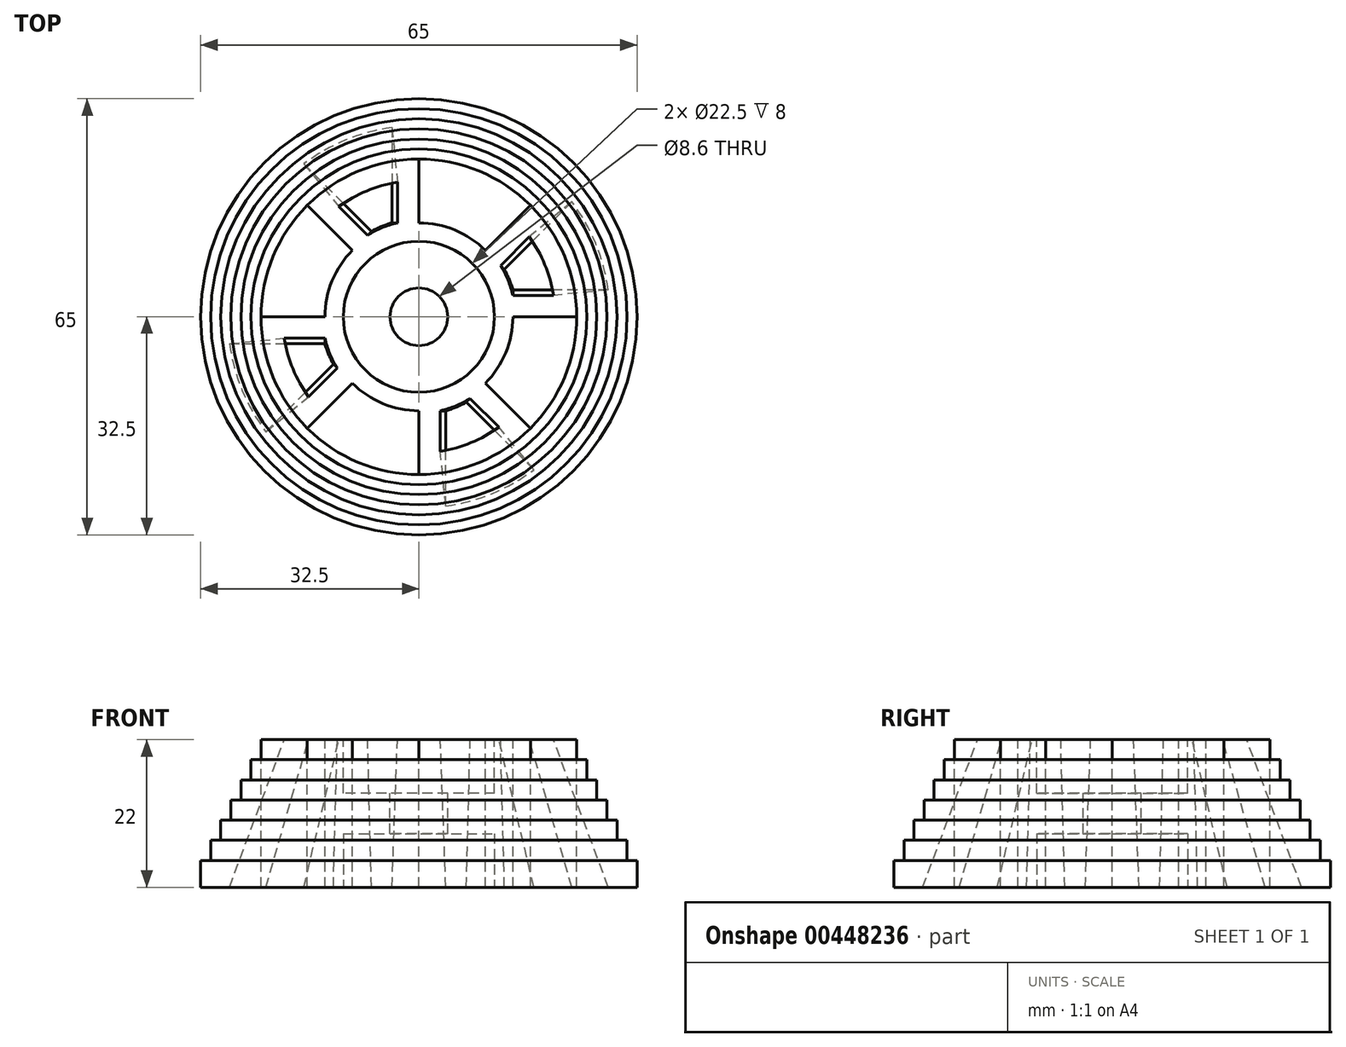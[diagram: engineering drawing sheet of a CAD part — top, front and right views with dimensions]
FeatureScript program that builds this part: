
annotation { "Feature Type Name" : "Feature", "Feature Type Description" : "" }
export const myFeature = defineFeature(function(context is Context, id is Id, definition is map)
    precondition{}
    {
        {
            var Q0;
            Q0=qCreatedBy(makeId("Top.planeOp"),FACE);
            var sketch = newSketch(context, id + "F0", { "sketchPlane" : qUnion([Q0])});
            skCircle(sketch, "E0", {"center": v(0, 0) * mm, "radius": 32.5 * mm});
            skCircle(sketch, "E1.0", {"center": v(0, 0) * mm, "radius": 31 * mm});
            skCircle(sketch, "E2.0", {"center": v(0, 0) * mm, "radius": 29.5 * mm});
            skCircle(sketch, "E3.0", {"center": v(0, 0) * mm, "radius": 28 * mm});
            skCircle(sketch, "E4.0", {"center": v(0, 0) * mm, "radius": 26.5 * mm});
            skCircle(sketch, "E5.0", {"center": v(0, 0) * mm, "radius": 25 * mm});
            skCircle(sketch, "E6.0", {"center": v(0, 0) * mm, "radius": 23.5 * mm});
            skSolve(sketch);
        }
        {
            var Q0;
            Q0 = qSketchRegion(id + "F0", true);
            extrude(context, id + "F1", {"entities" : qUnion([Q0]), "depth" : 4 * mm, "offsetDistance" : 25 * mm});
        }
        {
            var Q0;
            Q0=makeQuery(id+"F0.imprint","IMPRINT",FACE,{"disambiguationData":[TD([[makeQuery(id+"F0.imprint","IMPRINT",EDGE,{"derivedFrom":sQuery(id+"F0.wireOp",EDGE,"E1.0")}),1.0]])]});
            extrude(context, id + "F2", {"entities" : qUnion([Q0]), "operationType" : NewBodyOperationType.ADD, "depth" : 7 * mm, "offsetDistance" : 25 * mm});
        }
        {
            var Q0;
            Q0=makeQuery(id+"F0.imprint","IMPRINT",FACE,{"disambiguationData":[TD([[makeQuery(id+"F0.imprint","IMPRINT",EDGE,{"derivedFrom":sQuery(id+"F0.wireOp",EDGE,"E2.0")}),1.0]])]});
            extrude(context, id + "F3", {"entities" : qUnion([Q0]), "operationType" : NewBodyOperationType.ADD, "depth" : 10 * mm, "offsetDistance" : 25 * mm});
        }
        {
            var Q0;
            Q0=makeQuery(id+"F0.imprint","IMPRINT",FACE,{"disambiguationData":[TD([[makeQuery(id+"F0.imprint","IMPRINT",EDGE,{"derivedFrom":sQuery(id+"F0.wireOp",EDGE,"E3.0")}),1.0]])]});
            extrude(context, id + "F4", {"entities" : qUnion([Q0]), "operationType" : NewBodyOperationType.ADD, "depth" : 13 * mm, "offsetDistance" : 25 * mm});
        }
        {
            var Q0;
            Q0=makeQuery(id+"F0.imprint","IMPRINT",FACE,{"disambiguationData":[TD([[makeQuery(id+"F0.imprint","IMPRINT",EDGE,{"derivedFrom":sQuery(id+"F0.wireOp",EDGE,"E4.0")}),1.0]])]});
            extrude(context, id + "F5", {"entities" : qUnion([Q0]), "operationType" : NewBodyOperationType.ADD, "depth" : 16 * mm, "offsetDistance" : 25 * mm});
        }
        {
            var Q0;
            Q0=makeQuery(id+"F0.imprint","IMPRINT",FACE,{"disambiguationData":[TD([[makeQuery(id+"F0.imprint","IMPRINT",EDGE,{"derivedFrom":sQuery(id+"F0.wireOp",EDGE,"E5.0")}),1.0]])]});
            extrude(context, id + "F6", {"entities" : qUnion([Q0]), "operationType" : NewBodyOperationType.ADD, "depth" : 19 * mm, "offsetDistance" : 25 * mm});
        }
        {
            var Q0;
            Q0=makeQuery(id+"F0.imprint","IMPRINT",FACE,{"disambiguationData":[TD([[makeQuery(id+"F0.imprint","IMPRINT",EDGE,{"derivedFrom":sQuery(id+"F0.wireOp",EDGE,"E6.0")}),1.0]])]});
            extrude(context, id + "F7", {"entities" : qUnion([Q0]), "operationType" : NewBodyOperationType.ADD, "depth" : 22 * mm, "offsetDistance" : 25 * mm});
        }
        {
            var Q0;
            Q0=makeQuery(id+"F7.opExtrude","CAP_FACE",FACE,{"disambiguationData":[OSD([sQuery(id+"F0.wireOp",EDGE,"E6.0")])],"isStart":false});
            var sketch = newSketch(context, id + "F8", { "sketchPlane" : qUnion([Q0])});
            skCircle(sketch, "E7", {"center": v(0, 0) * mm, "radius": 14 * mm});
            skLineSegment(sketch, "E8", {"start": v(0, 0) * mm, "end": v(-25.46, 25.46) * mm, "construction": true});
            skLineSegment(sketch, "E9", {"start": v(-9.9, 9.9) * mm, "end": v(-25.46, 25.46) * mm});
            skLineSegment(sketch, "E10", {"start": v(-36, 0) * mm, "end": v(-14, 0) * mm});
            skArc(sketch, "E11", {"start": v(-36, 0) * mm, "mid": v(-33.26, 13.78) * mm, "end": v(-25.46, 25.46) * mm});
            skLineSegment(sketch, "E12.1.0", {"start": v(0, 0) * mm, "end": v(-25.46, -25.46) * mm, "construction": true});
            skLineSegment(sketch, "E12.2.0", {"start": v(0, 0) * mm, "end": v(25.46, -25.46) * mm, "construction": true});
            skLineSegment(sketch, "E13.1.0", {"start": v(0, -36) * mm, "end": v(0, -14) * mm});
            skLineSegment(sketch, "E13.2.0", {"start": v(36, 0) * mm, "end": v(14, 0) * mm});
            skLineSegment(sketch, "E14.2.3.0", {"start": v(0, 0) * mm, "end": v(25.46, 25.46) * mm, "construction": true});
            skLineSegment(sketch, "E15.1.3.0", {"start": v(0, 36) * mm, "end": v(0, 14) * mm});
            skArc(sketch, "E16", {"start": v(0, 36) * mm, "mid": v(13.78, 33.26) * mm, "end": v(25.46, 25.46) * mm});
            skArc(sketch, "E17", {"start": v(36, 0) * mm, "mid": v(33.26, -13.78) * mm, "end": v(25.46, -25.46) * mm});
            skArc(sketch, "E18", {"start": v(0, -36) * mm, "mid": v(-13.78, -33.26) * mm, "end": v(-25.46, -25.46) * mm});
            skLineSegment(sketch, "E19", {"start": v(9.9, 9.9) * mm, "end": v(25.46, 25.46) * mm});
            skLineSegment(sketch, "E20", {"start": v(9.9, -9.9) * mm, "end": v(25.46, -25.46) * mm});
            skLineSegment(sketch, "E21", {"start": v(-9.9, -9.9) * mm, "end": v(-25.46, -25.46) * mm});
            skSolve(sketch);
        }
        {
            var Q0;
            {var subQ0=sQuery(id+"F8.wireOp",EDGE,"E11");Q0=makeQuery(id+"F8.imprint","IMPRINT",FACE,{"disambiguationData":[TD([[makeQuery(id+"F8.imprint","IMPRINT",EDGE,{"derivedFrom":subQ0}),-1.0]])]});}
            var Q1;
            {var subQ0=sQuery(id+"F8.wireOp",EDGE,"E9");var subQ1=sQuery(id+"F8.wireOp",EDGE,"E7");var subQ2=makeQuery(id+"F8.imprint","INTERSECT",VERTEX,{"derivedFrom":[subQ1,subQ0]});Q1=makeQuery(id+"F8.imprint","IMPRINT",FACE,{"disambiguationData":[TD([[makeQuery(id+"F8.imprint","IMPRINT",EDGE,{"disambiguationData":[TD([[subQ2,-1.0]])],"derivedFrom":subQ1}),-1.0]])]});}
            var Q2;
            {var subQ0=sQuery(id+"F8.wireOp",EDGE,"E15.1.3.0");var subQ1=sQuery(id+"F8.wireOp",EDGE,"E7");var subQ2=makeQuery(id+"F8.imprint","INTERSECT",VERTEX,{"derivedFrom":[subQ1,subQ0]});Q2=makeQuery(id+"F8.imprint","IMPRINT",FACE,{"disambiguationData":[TD([[makeQuery(id+"F8.imprint","IMPRINT",EDGE,{"disambiguationData":[TD([[subQ2,1.0]])],"derivedFrom":subQ1}),-1.0]])]});}
            var Q3;
            {var subQ0=sQuery(id+"F8.wireOp",EDGE,"E16");Q3=makeQuery(id+"F8.imprint","IMPRINT",FACE,{"disambiguationData":[TD([[makeQuery(id+"F8.imprint","IMPRINT",EDGE,{"derivedFrom":subQ0}),-1.0]])]});}
            var Q4;
            {var subQ0=sQuery(id+"F8.wireOp",EDGE,"E13.2.0");var subQ1=sQuery(id+"F8.wireOp",EDGE,"E7");var subQ2=makeQuery(id+"F8.imprint","INTERSECT",VERTEX,{"derivedFrom":[subQ1,subQ0]});Q4=makeQuery(id+"F8.imprint","IMPRINT",FACE,{"disambiguationData":[TD([[makeQuery(id+"F8.imprint","IMPRINT",EDGE,{"disambiguationData":[TD([[subQ2,1.0]])],"derivedFrom":subQ1}),-1.0]])]});}
            var Q5;
            {var subQ0=sQuery(id+"F8.wireOp",EDGE,"E17");Q5=makeQuery(id+"F8.imprint","IMPRINT",FACE,{"disambiguationData":[TD([[makeQuery(id+"F8.imprint","IMPRINT",EDGE,{"derivedFrom":subQ0}),-1.0]])]});}
            var Q6;
            {var subQ0=sQuery(id+"F8.wireOp",EDGE,"E13.1.0");var subQ1=sQuery(id+"F8.wireOp",EDGE,"E7");var subQ2=makeQuery(id+"F8.imprint","INTERSECT",VERTEX,{"derivedFrom":[subQ1,subQ0]});Q6=makeQuery(id+"F8.imprint","IMPRINT",FACE,{"disambiguationData":[TD([[makeQuery(id+"F8.imprint","IMPRINT",EDGE,{"disambiguationData":[TD([[subQ2,1.0]])],"derivedFrom":subQ1}),-1.0]])]});}
            var Q7;
            {var subQ0=sQuery(id+"F8.wireOp",EDGE,"E18");Q7=makeQuery(id+"F8.imprint","IMPRINT",FACE,{"disambiguationData":[TD([[makeQuery(id+"F8.imprint","IMPRINT",EDGE,{"derivedFrom":subQ0}),-1.0]])]});}
            extrude(context, id + "F9", {"entities" : qUnion([Q0, Q1, Q2, Q3, Q4, Q5, Q6, Q7]), "operationType" : NewBodyOperationType.REMOVE, "oppositeDirection" : true, "depth" : 25 * mm, "offsetDistance" : 25 * mm});
        }
        {
            var Q0;
            Q0=makeQuery(id+"F7.opExtrude","CAP_FACE",FACE,{"disambiguationData":[OSD([sQuery(id+"F0.wireOp",EDGE,"E6.0")])],"isStart":false});
            var sketch = newSketch(context, id + "F10", { "sketchPlane" : qUnion([Q0])});
            skPoint(sketch, "E22", {"position": v(0, 0) * mm});
            skSolve(sketch);
        }
        {
            var Q0;
            Q0=sQuery(id+"F10.wireOp",VERTEX,"E22");
            var Q1;
            Q1=makeQuery(id+"F1.opExtrude","SWEPT_BODY",BODY,{"disambiguationData":[OSD([sQuery(id+"F0.wireOp",EDGE,"E0"),sQuery(id+"F0.wireOp",EDGE,"E1.0")])]});
            hole(context, id + "F11", {"style" : HoleStyle.C_BORE, "endStyle" : HoleEndStyle.THROUGH, "holeDiameter" : 8.6 * mm, "cBoreDiameter" : 22.5 * mm, "cBoreDepth" : 8 * mm, "isTappedThrough" : true, "tappedDepth" : 12 * mm, "tapClearance" : 3, "locations" : qUnion([Q0]), "scope" : qUnion([Q1])});
        }
        {
            var Q0;
            {var subQ0=sQuery(id+"F0.wireOp",EDGE,"E6.0");var subQ1=sQuery(id+"F0.wireOp",EDGE,"E5.0");var subQ2=sQuery(id+"F0.wireOp",EDGE,"E4.0");var subQ3=sQuery(id+"F0.wireOp",EDGE,"E3.0");var subQ4=sQuery(id+"F0.wireOp",EDGE,"E2.0");var subQ5=sQuery(id+"F0.wireOp",EDGE,"E1.0");Q0=makeQuery(id+"F7.boolean.opBoolean","MERGE",FACE,{"derivedFrom":[makeQuery(id+"F6.boolean.opBoolean","MERGE",FACE,{"derivedFrom":[makeQuery(id+"F5.boolean.opBoolean","MERGE",FACE,{"derivedFrom":[makeQuery(id+"F4.boolean.opBoolean","MERGE",FACE,{"derivedFrom":[makeQuery(id+"F3.boolean.opBoolean","MERGE",FACE,{"derivedFrom":[makeQuery(id+"F2.boolean.opBoolean","MERGE",FACE,{"derivedFrom":[makeQuery(id+"F1.opExtrude","CAP_FACE",FACE,{"disambiguationData":[OSD([sQuery(id+"F0.wireOp",EDGE,"E0"),subQ5])],"isStart":true}),makeQuery(id+"F2.opExtrude","CAP_FACE",FACE,{"disambiguationData":[OSD([subQ5,subQ4])],"isStart":true})]}),makeQuery(id+"F3.opExtrude","CAP_FACE",FACE,{"disambiguationData":[OSD([subQ4,subQ3])],"isStart":true})]}),makeQuery(id+"F4.opExtrude","CAP_FACE",FACE,{"disambiguationData":[OSD([subQ3,subQ2])],"isStart":true})]}),makeQuery(id+"F5.opExtrude","CAP_FACE",FACE,{"disambiguationData":[OSD([subQ2,subQ1])],"isStart":true})]}),makeQuery(id+"F6.opExtrude","CAP_FACE",FACE,{"disambiguationData":[OSD([subQ1,subQ0])],"isStart":true})]}),makeQuery(id+"F7.opExtrude","CAP_FACE",FACE,{"disambiguationData":[OSD([subQ0])],"isStart":true})]});}
            var sketch = newSketch(context, id + "F12", { "sketchPlane" : qUnion([Q0])});
            skPoint(sketch, "E23", {"position": v(0, 0) * mm});
            skCircle(sketch, "E24", {"center": v(0, 0) * mm, "radius": 11.25 * mm});
            skSolve(sketch);
        }
        {
            var Q0;
            Q0=makeQuery(id+"F12.imprint","IMPRINT",FACE,{"disambiguationData":[TD([[makeQuery(id+"F12.imprint","IMPRINT",EDGE,{"derivedFrom":sQuery(id+"F12.wireOp",EDGE,"E24")}),1.0]])]});
            extrude(context, id + "F13", {"entities" : qUnion([Q0]), "operationType" : NewBodyOperationType.REMOVE, "oppositeDirection" : true, "depth" : 8 * mm, "offsetDistance" : 25 * mm});
        }
        {
            var Q0;
            {var subQ0=sQuery(id+"F0.wireOp",EDGE,"E6.0");var subQ1=sQuery(id+"F0.wireOp",EDGE,"E5.0");var subQ2=sQuery(id+"F0.wireOp",EDGE,"E4.0");var subQ3=sQuery(id+"F0.wireOp",EDGE,"E3.0");var subQ4=sQuery(id+"F0.wireOp",EDGE,"E2.0");var subQ5=sQuery(id+"F0.wireOp",EDGE,"E1.0");Q0=makeQuery(id+"F7.boolean.opBoolean","MERGE",FACE,{"derivedFrom":[makeQuery(id+"F6.boolean.opBoolean","MERGE",FACE,{"derivedFrom":[makeQuery(id+"F5.boolean.opBoolean","MERGE",FACE,{"derivedFrom":[makeQuery(id+"F4.boolean.opBoolean","MERGE",FACE,{"derivedFrom":[makeQuery(id+"F3.boolean.opBoolean","MERGE",FACE,{"derivedFrom":[makeQuery(id+"F2.boolean.opBoolean","MERGE",FACE,{"derivedFrom":[makeQuery(id+"F1.opExtrude","CAP_FACE",FACE,{"disambiguationData":[OSD([sQuery(id+"F0.wireOp",EDGE,"E0"),subQ5])],"isStart":true}),makeQuery(id+"F2.opExtrude","CAP_FACE",FACE,{"disambiguationData":[OSD([subQ5,subQ4])],"isStart":true})]}),makeQuery(id+"F3.opExtrude","CAP_FACE",FACE,{"disambiguationData":[OSD([subQ4,subQ3])],"isStart":true})]}),makeQuery(id+"F4.opExtrude","CAP_FACE",FACE,{"disambiguationData":[OSD([subQ3,subQ2])],"isStart":true})]}),makeQuery(id+"F5.opExtrude","CAP_FACE",FACE,{"disambiguationData":[OSD([subQ2,subQ1])],"isStart":true})]}),makeQuery(id+"F6.opExtrude","CAP_FACE",FACE,{"disambiguationData":[OSD([subQ1,subQ0])],"isStart":true})]}),makeQuery(id+"F7.opExtrude","CAP_FACE",FACE,{"disambiguationData":[OSD([subQ0])],"isStart":true})]});}
            var sketch = newSketch(context, id + "F14", { "sketchPlane" : qUnion([Q0])});
            skLineSegment(sketch, "E25.0", {"start": v(-7.07, -12.73) * mm, "end": v(-17.12, -22.78) * mm});
            skArc(sketch, "E25.1", {"start": v(-4, -28.22) * mm, "mid": v(-10.9, -26.33) * mm, "end": v(-17.12, -22.78) * mm});
            skLineSegment(sketch, "E25.2", {"start": v(-4, -28.22) * mm, "end": v(-4, -14) * mm});
            skLineSegment(sketch, "E26.1.0", {"start": v(12.73, -7.07) * mm, "end": v(22.78, -17.12) * mm});
            skArc(sketch, "E26.1.1", {"start": v(28.22, -4) * mm, "mid": v(26.33, -10.9) * mm, "end": v(22.78, -17.12) * mm});
            skLineSegment(sketch, "E26.1.2", {"start": v(28.22, -4) * mm, "end": v(14, -4) * mm});
            skLineSegment(sketch, "E26.2.0", {"start": v(7.07, 12.73) * mm, "end": v(17.12, 22.78) * mm});
            skArc(sketch, "E26.2.1", {"start": v(4, 28.22) * mm, "mid": v(10.9, 26.33) * mm, "end": v(17.12, 22.78) * mm});
            skLineSegment(sketch, "E26.2.2", {"start": v(4, 28.22) * mm, "end": v(4, 14) * mm});
            skLineSegment(sketch, "E26.3.0", {"start": v(-12.73, 7.07) * mm, "end": v(-22.78, 17.12) * mm});
            skArc(sketch, "E26.3.1", {"start": v(-28.22, 4) * mm, "mid": v(-26.33, 10.9) * mm, "end": v(-22.78, 17.12) * mm});
            skLineSegment(sketch, "E26.3.2", {"start": v(-28.22, 4) * mm, "end": v(-14, 4) * mm});
            skArc(sketch, "E27", {"start": v(-4, -14) * mm, "mid": v(-5.57, -13.45) * mm, "end": v(-7.07, -12.73) * mm});
            skArc(sketch, "E28", {"start": v(-14, 4) * mm, "mid": v(-13.45, 5.57) * mm, "end": v(-12.73, 7.07) * mm});
            skArc(sketch, "E29", {"start": v(4, 14) * mm, "mid": v(5.57, 13.45) * mm, "end": v(7.07, 12.73) * mm});
            skArc(sketch, "E30", {"start": v(14, -4) * mm, "mid": v(13.45, -5.57) * mm, "end": v(12.73, -7.07) * mm});
            skSolve(sketch);
        }
        {
            var Q0;
            Q0=makeQuery(id+"F7.opExtrude","CAP_FACE",FACE,{"disambiguationData":[OSD([sQuery(id+"F0.wireOp",EDGE,"E6.0")])],"isStart":false});
            var sketch = newSketch(context, id + "F15", { "sketchPlane" : qUnion([Q0])});
            skLineSegment(sketch, "E31.0", {"start": v(-12.16, -7.64) * mm, "end": v(-16.44, -11.91) * mm});
            skArc(sketch, "E31.1", {"start": v(-20.05, -3.2) * mm, "mid": v(-18.75, -7.77) * mm, "end": v(-16.44, -11.91) * mm});
            skLineSegment(sketch, "E31.2", {"start": v(-20.05, -3.2) * mm, "end": v(-14, -3.2) * mm});
            skArc(sketch, "E32", {"start": v(-12.16, -7.64) * mm, "mid": v(-13.27, -5.5) * mm, "end": v(-14, -3.2) * mm});
            skArc(sketch, "E33.1.0", {"start": v(3.2, -20.05) * mm, "mid": v(7.77, -18.75) * mm, "end": v(11.91, -16.44) * mm});
            skLineSegment(sketch, "E33.1.1", {"start": v(3.2, -20.05) * mm, "end": v(3.2, -14) * mm});
            skLineSegment(sketch, "E33.1.2", {"start": v(7.64, -12.16) * mm, "end": v(11.91, -16.44) * mm});
            skArc(sketch, "E33.1.3", {"start": v(7.64, -12.16) * mm, "mid": v(5.5, -13.27) * mm, "end": v(3.2, -14) * mm});
            skArc(sketch, "E33.2.0", {"start": v(20.05, 3.2) * mm, "mid": v(18.75, 7.77) * mm, "end": v(16.44, 11.91) * mm});
            skLineSegment(sketch, "E33.2.1", {"start": v(20.05, 3.2) * mm, "end": v(14, 3.2) * mm});
            skLineSegment(sketch, "E33.2.2", {"start": v(12.16, 7.64) * mm, "end": v(16.44, 11.91) * mm});
            skArc(sketch, "E33.2.3", {"start": v(12.16, 7.64) * mm, "mid": v(13.27, 5.5) * mm, "end": v(14, 3.2) * mm});
            skArc(sketch, "E33.3.0", {"start": v(-3.2, 20.05) * mm, "mid": v(-7.77, 18.75) * mm, "end": v(-11.91, 16.44) * mm});
            skLineSegment(sketch, "E33.3.1", {"start": v(-3.2, 20.05) * mm, "end": v(-3.2, 14) * mm});
            skLineSegment(sketch, "E33.3.2", {"start": v(-7.64, 12.16) * mm, "end": v(-11.91, 16.44) * mm});
            skArc(sketch, "E33.3.3", {"start": v(-7.64, 12.16) * mm, "mid": v(-5.5, 13.27) * mm, "end": v(-3.2, 14) * mm});
            skSolve(sketch);
        }
        {
            var Q1;
            Q1=makeQuery(id+"F14.imprint","IMPRINT",FACE,{"disambiguationData":[TD([[makeQuery(id+"F14.imprint","IMPRINT",EDGE,{"derivedFrom":sQuery(id+"F14.wireOp",EDGE,"E26.2.0")}),1.0]])]});
            var Q2;
            Q2=makeQuery(id+"F15.imprint","IMPRINT",FACE,{"disambiguationData":[TD([[makeQuery(id+"F15.imprint","IMPRINT",EDGE,{"derivedFrom":sQuery(id+"F15.wireOp",EDGE,"E33.1.0")}),1.0]])]});
            loft(context, id + "F16", {"operationType" : NewBodyOperationType.REMOVE, "sheetProfilesArray" : [{ "sheetProfileEntities" : qUnion([Q1]) }, { "sheetProfileEntities" : qUnion([Q2]) }]});
        }
        {
            var Q1;
            Q1=makeQuery(id+"F14.imprint","IMPRINT",FACE,{"disambiguationData":[TD([[makeQuery(id+"F14.imprint","IMPRINT",EDGE,{"derivedFrom":sQuery(id+"F14.wireOp",EDGE,"E26.1.0")}),1.0]])]});
            var Q2;
            Q2=makeQuery(id+"F15.imprint","IMPRINT",FACE,{"disambiguationData":[TD([[makeQuery(id+"F15.imprint","IMPRINT",EDGE,{"derivedFrom":sQuery(id+"F15.wireOp",EDGE,"E33.2.0")}),1.0]])]});
            loft(context, id + "F17", {"operationType" : NewBodyOperationType.REMOVE, "sheetProfilesArray" : [{ "sheetProfileEntities" : qUnion([Q1]) }, { "sheetProfileEntities" : qUnion([Q2]) }]});
        }
        {
            var Q1;
            Q1=makeQuery(id+"F14.imprint","IMPRINT",FACE,{"disambiguationData":[TD([[makeQuery(id+"F14.imprint","IMPRINT",EDGE,{"derivedFrom":sQuery(id+"F14.wireOp",EDGE,"E25.0")}),1.0]])]});
            var Q2;
            Q2=makeQuery(id+"F15.imprint","IMPRINT",FACE,{"disambiguationData":[TD([[makeQuery(id+"F15.imprint","IMPRINT",EDGE,{"derivedFrom":sQuery(id+"F15.wireOp",EDGE,"E33.3.0")}),1.0]])]});
            loft(context, id + "F18", {"operationType" : NewBodyOperationType.REMOVE, "sheetProfilesArray" : [{ "sheetProfileEntities" : qUnion([Q1]) }, { "sheetProfileEntities" : qUnion([Q2]) }]});
        }
        {
            var Q1;
            Q1=makeQuery(id+"F14.imprint","IMPRINT",FACE,{"disambiguationData":[TD([[makeQuery(id+"F14.imprint","IMPRINT",EDGE,{"derivedFrom":sQuery(id+"F14.wireOp",EDGE,"E26.3.0")}),1.0]])]});
            var Q2;
            Q2=makeQuery(id+"F15.imprint","IMPRINT",FACE,{"disambiguationData":[TD([[makeQuery(id+"F15.imprint","IMPRINT",EDGE,{"derivedFrom":sQuery(id+"F15.wireOp",EDGE,"E31.0")}),-1.0]])]});
            loft(context, id + "F19", {"operationType" : NewBodyOperationType.REMOVE, "sheetProfilesArray" : [{ "sheetProfileEntities" : qUnion([Q1]) }, { "sheetProfileEntities" : qUnion([Q2]) }]});
        }
    });
